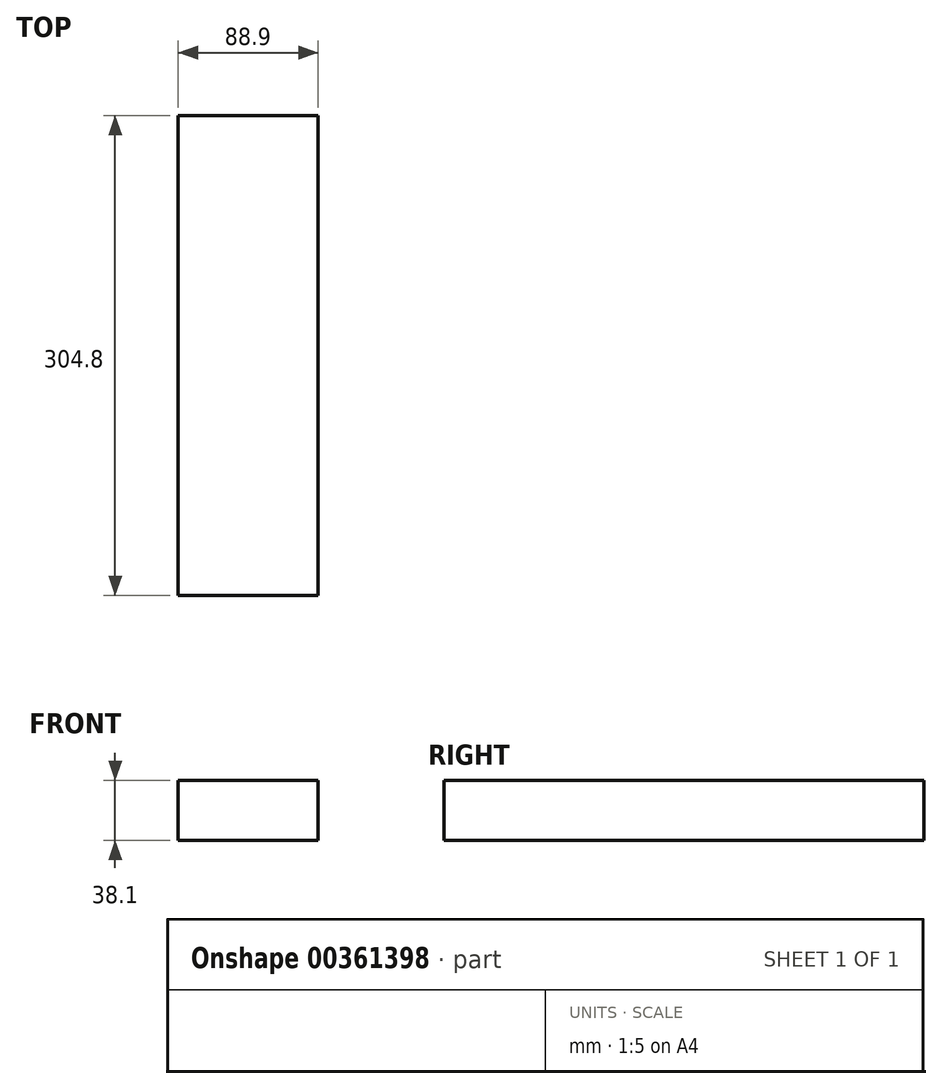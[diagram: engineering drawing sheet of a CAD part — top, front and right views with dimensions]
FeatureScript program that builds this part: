
annotation { "Feature Type Name" : "Feature", "Feature Type Description" : "" }
export const myFeature = defineFeature(function(context is Context, id is Id, definition is map)
    precondition{}
    {
        {
            var Q0;
            Q0=qCreatedBy(makeId("Front.planeOp"),FACE);
            var sketch = newSketch(context, id + "F0", { "sketchPlane" : qUnion([Q0])});
            skLineSegment(sketch, "E0.bottom", {"start": v(0, 0) * mm, "end": v(88.9, 0) * mm});
            skLineSegment(sketch, "E0.top", {"start": v(0, 38.1) * mm, "end": v(88.9, 38.1) * mm});
            skLineSegment(sketch, "E0.left", {"start": v(0, 0) * mm, "end": v(0, 38.1) * mm});
            skLineSegment(sketch, "E0.right", {"start": v(88.9, 0) * mm, "end": v(88.9, 38.1) * mm});
            skSolve(sketch);
        }
        {
            var Q0;
            Q0=makeQuery(id+"F0.imprint","IMPRINT",FACE,{"disambiguationData":[TD([[makeQuery(id+"F0.imprint","IMPRINT",EDGE,{"derivedFrom":sQuery(id+"F0.wireOp",EDGE,"E0.bottom")}),1.0]])]});
            extrude(context, id + "F1", {"entities" : qUnion([Q0]), "flatOperationType" : FlatOperationType.REMOVE, "oppositeDirection" : true, "offsetDistance" : 25.4 * mm, "depth" : 304.8 * mm, "domain" : OperationDomain.MODEL});
        }
    });
